# Revit family: S-753
name_source: partatom
category: Plumbing Fixtures
revit_build: Autodesk Revit 2015 (Build: 20140606_1530(x64)
units: mm (PartAtom-declared; Revit-internal decimal feet)

## types (6) — shared parameters
B = 52 mm
Description = CHANNEL GRID, ELEGANCE, FOR CHANNELS WIDTH 50
Grid = INOX AISI304
Manufacturer = Jimten
Material = INOX AISI304
Model = S-753
Type Comments = COMPATIBLE WITH VISIBLE OR THIN FRAMES
URL = http://www.jimten.com

## per-type parameters (varying)
| type | A | N_MatrizHuecos | Reference | Size |
| 50x350mm_ELEGANCE | 340 mm | 5 | 13536 | 350mm x 50mm |
| 50x550mm_ELEGANCE | 540 mm | 8 | 13556 | 550mm x 50mm |
| 50x650mm_ELEGANCE | 640 mm  [stored 2.09974 ft] | 10 | 13566 | 650mm x 50mm |
| 50x750mm_ELEGANCE | 740 mm | 12 | 13576 | 750mm x 50mm |
| 50x850mm_ELEGANCE | 840 mm | 13 | 13586 | 850mm x 50mm |
| 50x950mm_ELEGANCE | 940 mm | 15 | 13596 | 950mm x 50mm |

note: [stored X ft] marks values corroborated as IEEE doubles in the binary element streams (Revit-internal decimal feet)

## geometry (parser evidence)
native form markers: Blend x3, Sweep x2
no freeform markers — native parametric forms only
